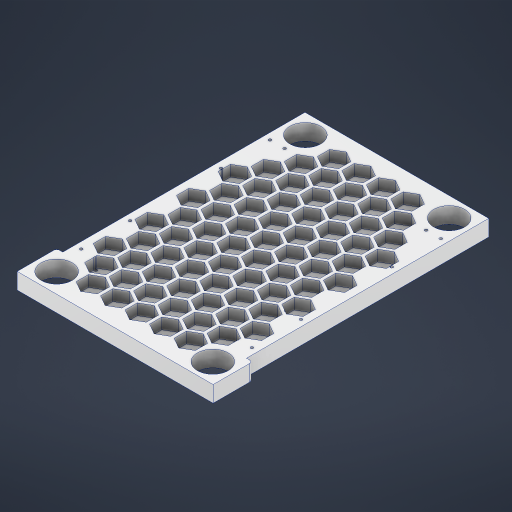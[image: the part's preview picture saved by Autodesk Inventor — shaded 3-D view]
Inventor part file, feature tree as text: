
AUTODESK INVENTOR PART (.ipt)
format: ipt  version: 2024 (Build 280153000, 153)  size: 1,011,200 bytes
history: native  units: in
note: dims shown in document units (in); Inventor stores cm internally (conversion verified against a paired STEP export)
features: extrude x5, sketch x4, hole x1, fillet x1
ambient origin geometry x8: Origin, YZ Plane, XZ Plane, XY Plane, X Axis, Y Axis, Z Axis, Center Point
bodies: Solid1 (feature_tree)
feature tree (11):
  extrude  "Extrusion1"  Depth=11.5in
  extrude  "Extrusion2"  Depth=0.66in
  hole  "Hole1"  [1 undecoded]
  extrude  "Extrusion10"  Depth=1.0in
  fillet  "Fillet5"  Radius=1.258in
  extrude  "Extrusion11"  Depth=1.0in
  extrude  "Extrusion12"  TaperAngle=0.0deg  [1 undecoded]
  sketch  "Sketch7"  dims[d0=7.5in d1=11.5in]
  sketch  "Sketch11"  dims[d2=0.66in d3=0.0in d5=0.8in]
  sketch  "Sketch12"  dims[d7=0.8in d9=0.8in]
  sketch  "Sketch13"  dims[d11=0.8in d12=1.258in d14=1.258in d15=1.258in d16=0.0in d17=0.0in d167=1.0in d168=1.0in d169=3.7105in d172=0.3in d173=0.3in d174=0.3in d175=0.3in d176=0.3in d177=0.3in d178=0.3in d179=0.3in d182=1.0in d183=1.0in d184=3.7105in d185=1.0in d186=1.0in d187=0.3in d188=0.3in d189=0.3in d190=0.3in d191=0.3in d192=0.3in d193=0.3in d194=0.3in d195=0.1378in d196=0.1378in d197=0.1378in d198=0.1378in d199=0.1378in d200=0.1378in d201=0.1378in d202=0.1378in d203=0.1378in d204=0.1378in d205=0.1378in d206=0.1378in d207=0.1378in d208=0.1378in d209=0.1378in d210=0.1378in d245=0.1122in d246=0.6in d247=0.185in d248=0.25in d249=0.5635in d250=1.0in d251=0.8108in d258=6.375in d259=0.25in d260=0.25in d264=1.258in d266=0.8125in d267=0.8125in d268=0.66in d269=0.0in d271=0.125in d272=0.25in d273=0.25in d274=0.8125in d276=0.8125in d277=2.25in d278=2.25in d279=2.25in d280=11.5in d281=7.5in d282=5.75in d283=3.75in d284=0.45in d285=0.0in d286=0.5in d294=0.5in d296=0.59in d297=0.75in d314=0.45in d315=0.0in d316=0.1in d317=0.5in d318=2.3622in d320=1.7in d321=2.7559in d323=1.0in]
note: 2 required parameter values undecoded (feature->parameter linkage not recoverable at this tier; creation-order binding heuristic only, values carry confidence <= 0.55)
